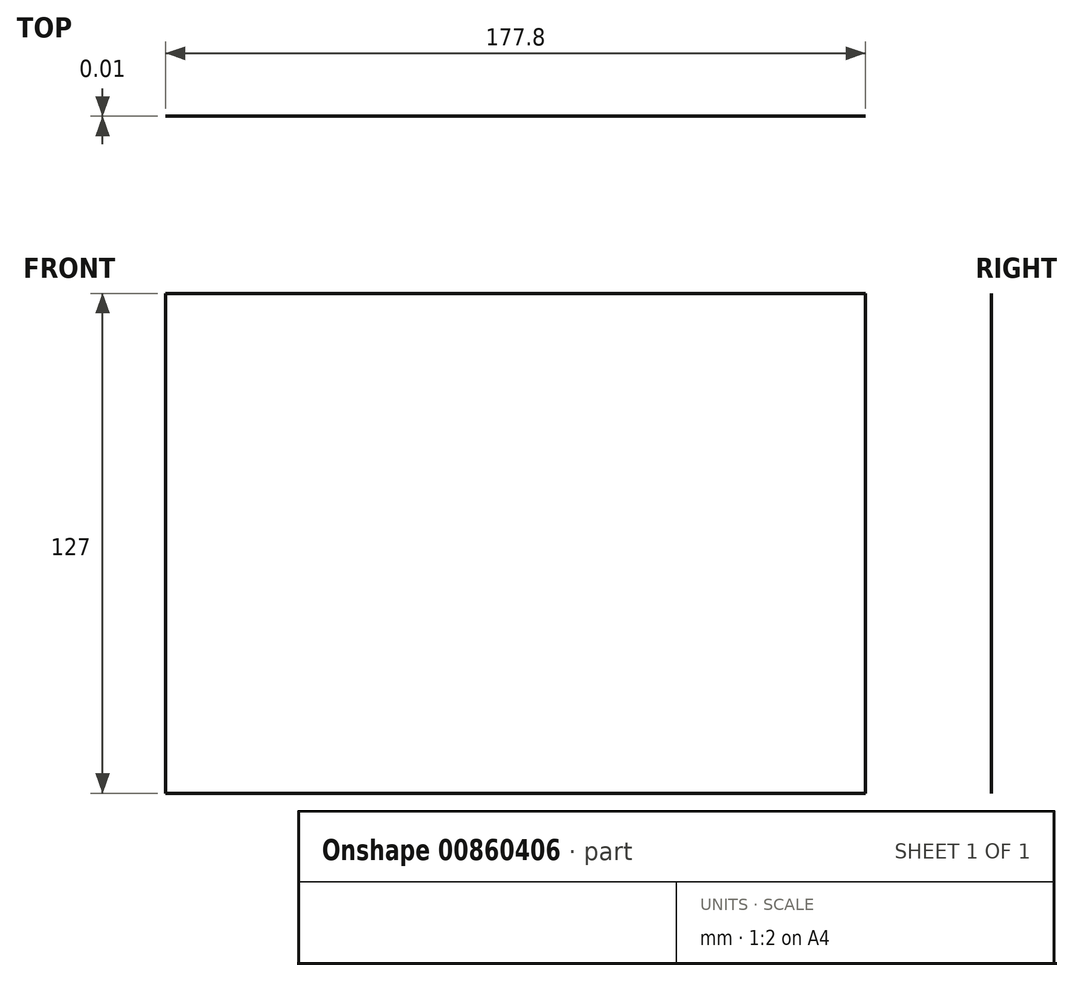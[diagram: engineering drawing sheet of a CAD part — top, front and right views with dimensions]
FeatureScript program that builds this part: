
annotation { "Feature Type Name" : "Feature", "Feature Type Description" : "" }
export const myFeature = defineFeature(function(context is Context, id is Id, definition is map)
    precondition{}
    {
        {
            var Q0;
            Q0=qCreatedBy(makeId("Front.planeOp"),FACE);
            var sketch = newSketch(context, id + "F0", { "sketchPlane" : qUnion([Q0])});
            skLineSegment(sketch, "E0.bottom", {"start": v(0, 0) * mm, "end": v(177.8, 0) * mm});
            skLineSegment(sketch, "E0.top", {"start": v(0, 127) * mm, "end": v(177.8, 127) * mm});
            skLineSegment(sketch, "E0.left", {"start": v(0, 0) * mm, "end": v(0, 127) * mm});
            skLineSegment(sketch, "E0.right", {"start": v(177.8, 0) * mm, "end": v(177.8, 127) * mm});
            skSolve(sketch);
        }
        {
            var Q0;
            Q0 = qSketchRegion(id + "F0", true);
            extrude(context, id + "F1", {"entities" : qUnion([Q0]), "depth" : 1 / 101.6 * mm, "offsetDistance" : 25.4 * mm});
        }
    });
